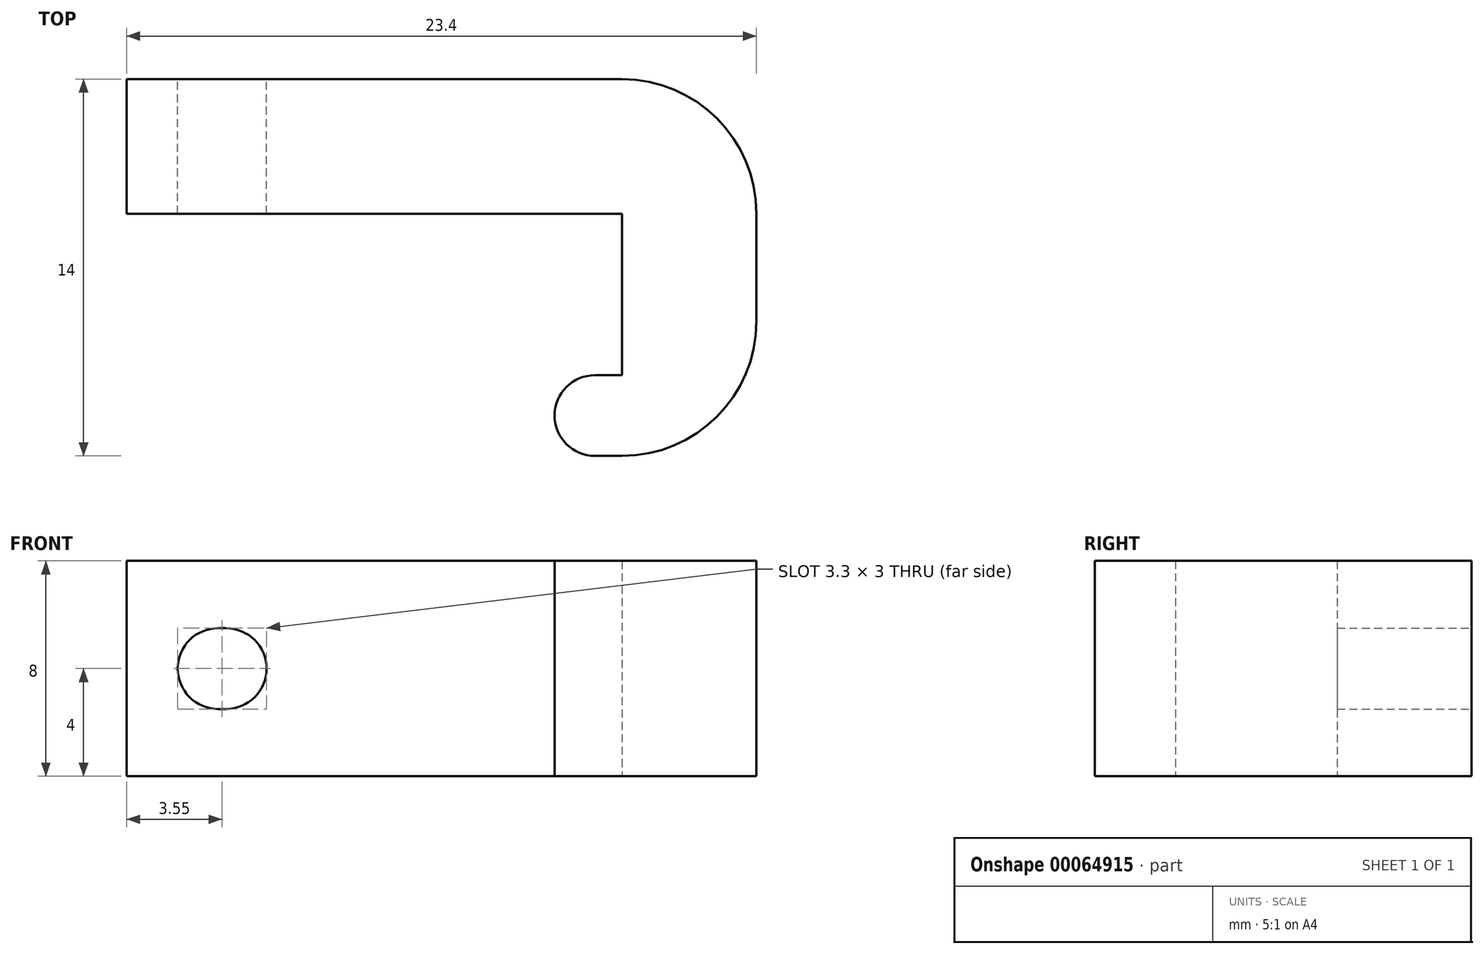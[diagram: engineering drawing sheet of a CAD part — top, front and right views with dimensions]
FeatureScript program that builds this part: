
annotation { "Feature Type Name" : "Feature", "Feature Type Description" : "" }
export const myFeature = defineFeature(function(context is Context, id is Id, definition is map)
    precondition{}
    {
        {
            var Q0;
            Q0=qCreatedBy(makeId("Top.planeOp"),FACE);
            var sketch = newSketch(context, id + "F0", { "sketchPlane" : qUnion([Q0])});
            skLineSegment(sketch, "E0", {"start": v(0, 0) * mm, "end": v(5, 0) * mm});
            skLineSegment(sketch, "E1", {"start": v(5, 0) * mm, "end": v(5, 14) * mm});
            skLineSegment(sketch, "E2", {"start": v(5, 14) * mm, "end": v(-18, 14) * mm});
            skLineSegment(sketch, "E3", {"start": v(-18, 14) * mm, "end": v(-18, 9) * mm});
            skLineSegment(sketch, "E4", {"start": v(-18, 9) * mm, "end": v(0, 9) * mm});
            skLineSegment(sketch, "E5", {"start": v(0, 9) * mm, "end": v(0, 3) * mm});
            skLineSegment(sketch, "E6", {"start": v(0, 3) * mm, "end": v(-1, 3) * mm});
            skLineSegment(sketch, "E7", {"start": v(0, 0) * mm, "end": v(-1, 0) * mm});
            skArc(sketch, "E8", {"start": v(-1, 3) * mm, "mid": v(-2.5, 1.5) * mm, "end": v(-1, 0) * mm});
            skSolve(sketch);
        }
        {
            var Q0;
            Q0=qSketchRegion(id+"F0",true);
            extrude(context, id + "F1", {"entities" : qUnion([Q0]), "depth" : 8 * mm});
        }
        {
            var Q0;
            Q0=makeQuery(id+"F1.opExtrude","SWEPT_FACE",FACE,{"disambiguationData":[OSD([sQuery(id+"F0.wireOp",EDGE,"E2")])]});
            var sketch = newSketch(context, id + "F2", { "sketchPlane" : qUnion([Q0])});
            skCircle(sketch, "E9", {"center": v(15, 4) * mm, "radius": 1.5 * mm});
            skLineSegment(sketch, "E10", {"start": v(15, 8) * mm, "end": v(15, 0) * mm});
            skCircle(sketch, "E11", {"center": v(14.7, 4) * mm, "radius": 1.5 * mm});
            skLineSegment(sketch, "E12", {"start": v(14.7, 5.5) * mm, "end": v(15, 5.5) * mm});
            skLineSegment(sketch, "E13", {"start": v(14.7, 2.5) * mm, "end": v(15, 2.5) * mm});
            skSolve(sketch);
        }
        {
            var Q0;
            {var subQ0=sQuery(id+"F2.wireOp",EDGE,"E10");var subQ4=sQuery(id+"F2.wireOp",EDGE,"E11");var subQ5=makeQuery(id+"F2.imprint","INTERSECT",VERTEX,{"disambiguationData":[OD(0.0)],"derivedFrom":[subQ0,subQ4]});Q0=makeQuery(id+"F2.imprint","IMPRINT",FACE,{"disambiguationData":[TD([[makeQuery(id+"F2.imprint","IMPRINT",EDGE,{"disambiguationData":[TD([[subQ5,1.0]])],"derivedFrom":subQ4}),-1.0]])]});}
            var Q1;
            {var subQ0=sQuery(id+"F2.wireOp",EDGE,"E11");var subQ1=sQuery(id+"F2.wireOp",EDGE,"E9");var subQ2=makeQuery(id+"F2.imprint","INTERSECT",VERTEX,{"disambiguationData":[OD(0.0)],"derivedFrom":[subQ1,subQ0]});Q1=makeQuery(id+"F2.imprint","IMPRINT",FACE,{"disambiguationData":[TD([[makeQuery(id+"F2.imprint","IMPRINT",EDGE,{"disambiguationData":[TD([[subQ2,-1.0]])],"derivedFrom":subQ1}),1.0]])]});}
            var Q2;
            {var subQ0=sQuery(id+"F2.wireOp",EDGE,"E11");var subQ1=sQuery(id+"F2.wireOp",EDGE,"E9");var subQ2=makeQuery(id+"F2.imprint","INTERSECT",VERTEX,{"disambiguationData":[OD(0.0)],"derivedFrom":[subQ1,subQ0]});Q2=makeQuery(id+"F2.imprint","IMPRINT",FACE,{"disambiguationData":[TD([[makeQuery(id+"F2.imprint","IMPRINT",EDGE,{"disambiguationData":[TD([[subQ2,-1.0]])],"derivedFrom":subQ1}),-1.0]])]});}
            var Q3;
            {var subQ0=sQuery(id+"F2.wireOp",EDGE,"E11");var subQ1=sQuery(id+"F2.wireOp",EDGE,"E10");var subQ2=makeQuery(id+"F2.imprint","INTERSECT",VERTEX,{"disambiguationData":[OD(0.0)],"derivedFrom":[subQ1,subQ0]});Q3=makeQuery(id+"F2.imprint","IMPRINT",FACE,{"disambiguationData":[TD([[makeQuery(id+"F2.imprint","IMPRINT",EDGE,{"disambiguationData":[TD([[subQ2,-1.0]])],"derivedFrom":subQ1}),1.0]])]});}
            var Q4;
            {var subQ1=sQuery(id+"F2.wireOp",EDGE,"E9");var subQ3=sQuery(id+"F2.wireOp",EDGE,"E11");var subQ4=makeQuery(id+"F2.imprint","INTERSECT",VERTEX,{"disambiguationData":[OD(0.0)],"derivedFrom":[subQ1,subQ3]});Q4=makeQuery(id+"F2.imprint","IMPRINT",FACE,{"disambiguationData":[TD([[makeQuery(id+"F2.imprint","IMPRINT",EDGE,{"disambiguationData":[TD([[subQ4,1.0]])],"derivedFrom":subQ3}),-1.0]])]});}
            var Q5;
            {var subQ1=sQuery(id+"F2.wireOp",EDGE,"E9");var subQ3=sQuery(id+"F2.wireOp",EDGE,"E11");var subQ4=makeQuery(id+"F2.imprint","INTERSECT",VERTEX,{"disambiguationData":[OD(1.0)],"derivedFrom":[subQ1,subQ3]});Q5=makeQuery(id+"F2.imprint","IMPRINT",FACE,{"disambiguationData":[TD([[makeQuery(id+"F2.imprint","IMPRINT",EDGE,{"disambiguationData":[TD([[subQ4,-1.0]])],"derivedFrom":subQ3}),-1.0]])]});}
            var Q6;
            {var subQ0=sQuery(id+"F2.wireOp",EDGE,"E12");Q6=makeQuery(id+"F2.imprint","IMPRINT",FACE,{"disambiguationData":[TD([[makeQuery(id+"F2.imprint","IMPRINT",EDGE,{"derivedFrom":subQ0}),-1.0]])]});}
            var Q7;
            {var subQ0=sQuery(id+"F2.wireOp",EDGE,"E13");Q7=makeQuery(id+"F2.imprint","IMPRINT",FACE,{"disambiguationData":[TD([[makeQuery(id+"F2.imprint","IMPRINT",EDGE,{"derivedFrom":subQ0}),1.0]])]});}
            extrude(context, id + "F3", {"entities" : qUnion([Q0, Q1, Q2, Q3, Q4, Q5, Q6, Q7]), "operationType" : NewBodyOperationType.REMOVE, "oppositeDirection" : true, "depth" : 25 * mm});
        }
        {
            var Q0;
            Q0=makeQuery(id+"F1.opExtrude","SWEPT_EDGE",EDGE,{"disambiguationData":[OSD([sQuery(id+"F0.wireOp",EDGE,"E1"),sQuery(id+"F0.wireOp",EDGE,"E2")])]});
            var Q1;
            Q1=makeQuery(id+"F1.opExtrude","SWEPT_EDGE",EDGE,{"disambiguationData":[OSD([sQuery(id+"F0.wireOp",EDGE,"E0"),sQuery(id+"F0.wireOp",EDGE,"E1")])]});
            fillet(context, id + "F4", {"entities" : qUnion([Q0, Q1]), "radius" : 5 * mm, "tangentPropagation" : true, "allowEdgeOverflow" : false});
        }
        {
            var Q0;
            Q0=makeQuery(id+"F1.opExtrude","SWEPT_FACE",FACE,{"disambiguationData":[OSD([sQuery(id+"F0.wireOp",EDGE,"E3")])]});
            extrude(context, id + "F5", {"entities" : qUnion([Q0]), "operationType" : NewBodyOperationType.ADD, "depth" : .4 * mm});
        }
    });
